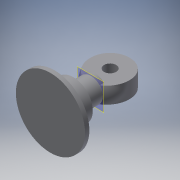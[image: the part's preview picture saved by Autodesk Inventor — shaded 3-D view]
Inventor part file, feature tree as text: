
AUTODESK INVENTOR PART (.ipt)
format: ipt  version: 2016 (Build 200138000, 138)  size: 360,960 bytes
history: native  units: in
note: dims shown in document units (in); Inventor stores cm internally (conversion verified against a paired STEP export)
features: extrude x6, sketch x6, fillet x4, plane x1
ambient origin geometry x8: Origin, YZ Plane, XZ Plane, XY Plane, X Axis, Y Axis, Z Axis, Center Point
bodies: Solid1 (feature_tree)
feature tree (17):
  extrude  "Extrusion1"  Depth=0.0394in TaperAngle=0.0deg
  extrude  "Extrusion2"  Depth=0.1693in TaperAngle=0.0deg
  extrude  "Extrusion3"  Depth=0.1969in TaperAngle=0.0deg
  plane  "Work Plane1"
  extrude  "Extrusion4"  Depth=0.3543in
  fillet  "Fillet1"  Radius=0.1496in
  extrude  "Extrusion5"  Depth=0.1772in
  extrude  "Extrusion6"  Depth=0.1732in
  fillet  "Fillet2"  Radius=0.1102in
  fillet  "Fillet3"  Radius=0.1732in
  fillet  "Fillet4"  Radius=0.3543in
  sketch  "Sketch1"  dims[d0=0.6299in d1=0.0394in d2=0.0in]
  sketch  "Sketch2"  dims[d3=0.3543in d4=0.1693in d5=0.0in]
  sketch  "Sketch3"  dims[d6=0.2205in d7=0.1969in d8=0.0in]
  sketch  "Sketch4"  dims[d9=-0.0394in d10=0.3543in d11=0.1496in]
  sketch  "Sketch5"  dims[d12=0.0748in d13=0.1772in]
  sketch  "Sketch6"  dims[d14=0.3543in d15=0.0in d16=0.1732in d18=0.1102in d19=0.1732in d20=0.3543in d21=0.0in d22=0.1181in d23=0.5906in d24=0.0in d25=0.0197in d26=0.0197in d27=0.0197in]
